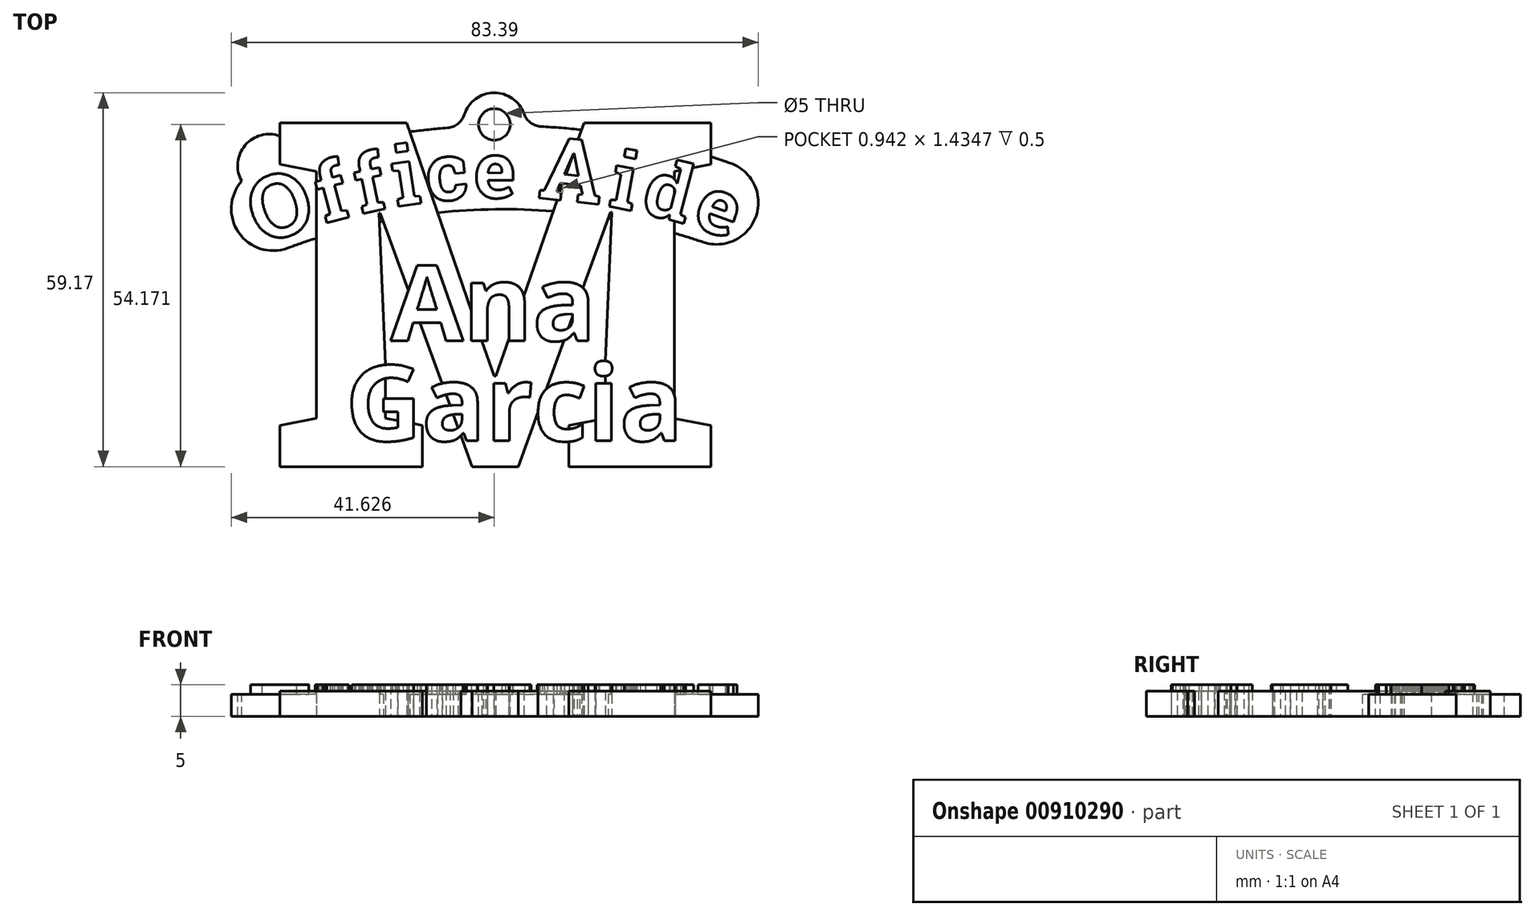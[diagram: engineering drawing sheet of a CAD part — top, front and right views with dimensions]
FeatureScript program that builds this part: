
annotation { "Feature Type Name" : "Feature", "Feature Type Description" : "" }
export const myFeature = defineFeature(function(context is Context, id is Id, definition is map)
    precondition{}
    {
        {
            var Q0;
            Q0=qCreatedBy(makeId("Top.planeOp"),FACE);
            var sketch = newSketch(context, id + "F0", { "sketchPlane" : qUnion([Q0])});
            skText(sketch, "E0", { "text": "M", "fontName": "RobotoSlab-Bold.ttf"});
            skCircle(sketch, "E1", {"center": v(0, 0) * mm, "radius": 110 * mm, "construction": true});
            const initialGuessF0  = {"E0": [-0.0375, 0.05744, 1, 0, 0.05512]};
            skSetInitialGuess(sketch, initialGuessF0);
            skSolve(sketch);
        }
        {
            var Q0;
            Q0=makeQuery(id+"F0.imprint","IMPRINT",FACE,{"disambiguationData":[TD([[makeQuery(id+"F0.imprint","IMPRINT",EDGE,{"derivedFrom":sQuery(id+"F0.wireOp",EDGE,"E0.sketch_text.stroke-0")}),-1.0]])]});
            extrude(context, id + "F1", {"entities" : qUnion([Q0]), "depth" : 4 * mm, "offsetDistance" : 25 * mm});
        }
        {
            var Q0;
            Q0=qCreatedBy(makeId("Top.planeOp"),FACE);
            var sketch = newSketch(context, id + "F2", { "sketchPlane" : qUnion([Q0])});
            skLineSegment(sketch, "E2", {"start": v(0, 0) * mm, "end": v(-1.2, 100) * mm, "construction": true});
            skText(sketch, "E3", { "text": "e", "fontName": "RobotoSlab-Bold.ttf"});
            skText(sketch, "E4", { "text": "c", "fontName": "RobotoSlab-Bold.ttf"});
            skLineSegment(sketch, "E5", {"start": v(0, 0) * mm, "end": v(-8.51, 99.64) * mm, "construction": true});
            skCircle(sketch, "E6", {"center": v(0, 0) * mm, "radius": 110 * mm, "construction": true});
            skLineSegment(sketch, "E7", {"start": v(0, 0) * mm, "end": v(79.9, 0) * mm, "construction": true});
            skText(sketch, "E8", { "text": "i", "fontName": "RobotoSlab-Bold.ttf"});
            skLineSegment(sketch, "E9", {"start": v(0, 0) * mm, "end": v(-14.63, 98.92) * mm, "construction": true});
            skLineSegment(sketch, "E10", {"start": v(0, 0) * mm, "end": v(-3.4, 0) * mm, "construction": true});
            skLineSegment(sketch, "E11", {"start": v(0, 0) * mm, "end": v(-20, 97.98) * mm, "construction": true});
            skLineSegment(sketch, "E12", {"start": v(0, 0) * mm, "end": v(-33.6, 94.18) * mm, "construction": true});
            skText(sketch, "E13", { "text": "f", "fontName": "RobotoSlab-Bold.ttf"});
            skText(sketch, "E14", { "text": "f", "fontName": "RobotoSlab-Bold.ttf"});
            skLineSegment(sketch, "E15", {"start": v(0, 0) * mm, "end": v(-25.73, 96.63) * mm, "construction": true});
            skText(sketch, "E16", { "text": "O", "fontName": "RobotoSlab-Bold.ttf"});
            skLineSegment(sketch, "E17", {"start": v(0, 0) * mm, "end": v(10.58, 99.44) * mm, "construction": true});
            skLineSegment(sketch, "E18", {"start": v(0, 0) * mm, "end": v(18.66, 98.24) * mm, "construction": true});
            skLineSegment(sketch, "E19", {"start": v(0, 0) * mm, "end": v(25.35, 96.73) * mm, "construction": true});
            skLineSegment(sketch, "E20", {"start": v(0, 0) * mm, "end": v(32.88, 94.44) * mm, "construction": true});
            skText(sketch, "E21", { "text": "A", "fontName": "RobotoSlab-Bold.ttf"});
            skText(sketch, "E22", { "text": "i", "fontName": "RobotoSlab-Bold.ttf"});
            skText(sketch, "E23", { "text": "d", "fontName": "RobotoSlab-Bold.ttf"});
            skText(sketch, "E24", { "text": "e", "fontName": "RobotoSlab-Bold.ttf"});
            const initialGuessF2  = {"E3": [-0.00468, 0.09995, 0.99993, 0.01194, 0.009], "E4": [-0.01205, 0.09934, 0.99637, 0.0851, 0.00918], "E8": [-0.01698, 0.09858, 0.98924, 0.14633, 0.0093], "E13": [-0.02271, 0.09743, 0.97978, 0.20006, 0.009], "E14": [-0.02845, 0.0959, 0.96634, 0.25726, 0.00919], "E16": [-0.03844, 0.09246, 0.94184, 0.33606, 0.01], "E21": [0.00533, 0.1, 0.99438, -0.10582, 0.01], "E22": [0.0164, 0.09867, 0.98244, -0.18659, 0.009], "E23": [0.0215, 0.09774, 0.96732, -0.25355, 0.009], "E24": [0.02959, 0.09559, 0.9444, -0.32878, 0.009]};
            skSetInitialGuess(sketch, initialGuessF2);
            skSolve(sketch);
        }
        {
            var Q0;
            Q0=qSketchRegion(id+"F2",true);
            extrude(context, id + "F3", {"entities" : qUnion([Q0]), "depth" : 5 * mm, "offsetDistance" : 25 * mm});
        }
        {
            var Q0;
            Q0=qCreatedBy(makeId("Top.planeOp"),FACE);
            var sketch = newSketch(context, id + "F4", { "sketchPlane" : qUnion([Q0])});
            skArc(sketch, "E25", {"start": v(31.54, 92.98) * mm, "mid": v(-1.4, 98.18) * mm, "end": v(-34.18, 92.04) * mm});
            skArc(sketch, "E26", {"start": v(35.79, 105.52) * mm, "mid": v(-1.6, 111.42) * mm, "end": v(-38.8, 104.46) * mm});
            skArc(sketch, "E27", {"start": v(-38.8, 104.46) * mm, "mid": v(-42.7, 95.95) * mm, "end": v(-34.18, 92.04) * mm});
            skArc(sketch, "E28", {"start": v(31.54, 92.98) * mm, "mid": v(39.93, 97.13) * mm, "end": v(35.79, 105.52) * mm});
            skSolve(sketch);
        }
        {
            var Q0;
            Q0=qSketchRegion(id+"F4",true);
            extrude(context, id + "F5", {"entities" : qUnion([Q0]), "operationType" : NewBodyOperationType.ADD, "depth" : 3.5 * mm, "offsetDistance" : 25 * mm});
        }
        {
            var Q0;
            Q0=makeQuery(id+"F5.opExtrude","CAP_FACE",FACE,{"disambiguationData":[OSD([sQuery(id+"F4.wireOp",EDGE,"E25"),sQuery(id+"F4.wireOp",EDGE,"E26"),sQuery(id+"F4.wireOp",EDGE,"E27"),sQuery(id+"F4.wireOp",EDGE,"E28")])],"isStart":false});
            var sketch = newSketch(context, id + "F6", { "sketchPlane" : qUnion([Q0])});
            skCircle(sketch, "E29", {"center": v(-37.1, 105.07) * mm, "radius": 5 * mm});
            skSolve(sketch);
        }
        {
            var Q0;
            {var subQ0=sQuery(id+"F6.wireOp",EDGE,"E29");var subQ1=makeQuery(id+"F5.opExtrude","CAP_EDGE",EDGE,{"disambiguationData":[OSD([sQuery(id+"F4.wireOp",EDGE,"E26")])],"isStart":false});var subQ2=makeQuery(id+"F6.imprint","INTERSECT",VERTEX,{"disambiguationData":[OD(0.0)],"derivedFrom":[subQ1,subQ0]});Q0=makeQuery(id+"F6.imprint","IMPRINT",FACE,{"disambiguationData":[TD([[makeQuery(id+"F6.imprint","IMPRINT",EDGE,{"disambiguationData":[TD([[subQ2,-1.0]])],"derivedFrom":subQ0}),1.0]])]});}
            extrude(context, id + "F7", {"entities" : qUnion([Q0]), "operationType" : NewBodyOperationType.ADD, "oppositeDirection" : true, "depth" : 3.5 * mm, "offsetDistance" : 25 * mm});
        }
        {
            var Q0;
            Q0=qCreatedBy(makeId("Top.planeOp"),FACE);
            var sketch = newSketch(context, id + "F8", { "sketchPlane" : qUnion([Q0])});
            skText(sketch, "E30", { "text": "Ana", "fontName": "OpenSans-Bold.ttf"});
            skText(sketch, "E31", { "text": "Garcia", "fontName": "OpenSans-Bold.ttf"});
            const initialGuessF8  = {"E30": [-0.0179, 0.07738, 1, 0, 0.012], "E31": [-0.02502, 0.06154, 1, 0, 0.012]};
            skSetInitialGuess(sketch, initialGuessF8);
            skSolve(sketch);
        }
        {
            var Q0;
            Q0=qSketchRegion(id+"F8",true);
            extrude(context, id + "F9", {"entities" : qUnion([Q0]), "operationType" : NewBodyOperationType.ADD, "depth" : 5 * mm, "offsetDistance" : 25 * mm});
        }
        {
            var Q0;
            Q0=qCreatedBy(makeId("Top.planeOp"),FACE);
            var sketch = newSketch(context, id + "F10", { "sketchPlane" : qUnion([Q0])});
            skLineSegment(sketch, "E32", {"start": v(-1.48, 71.98) * mm, "end": v(-1.48, 122.51) * mm, "construction": true});
            skCircle(sketch, "E33", {"center": v(-1.48, 111.61) * mm, "radius": 5 * mm});
            skSolve(sketch);
        }
        {
            var Q0;
            Q0=makeQuery(id+"F10.imprint","IMPRINT",FACE,{"disambiguationData":[TD([[makeQuery(id+"F10.imprint","IMPRINT",EDGE,{"derivedFrom":sQuery(id+"F10.wireOp",EDGE,"E33")}),1.0]])]});
            extrude(context, id + "F11", {"entities" : qUnion([Q0]), "operationType" : NewBodyOperationType.ADD, "depth" : 3.5 * mm, "offsetDistance" : 25 * mm});
        }
        {
            var Q0;
            {var subQ0=sQuery(id+"F4.wireOp",EDGE,"E25");var subQ1=sQuery(id+"F4.wireOp",EDGE,"E26");Q0=makeQuery(id+"F11.boolean.opBoolean","MERGE",FACE,{"derivedFrom":[makeQuery(id+"F5.boolean.opBoolean","SPLIT",FACE,{"disambiguationData":[TD([makeQuery(id+"F1.opExtrude","SWEPT_FACE",FACE,{"disambiguationData":[OSD([sQuery(id+"F0.wireOp",EDGE,"E0.sketch_text.stroke-17")])]})])],"derivedFrom":makeQuery(id+"F5.opExtrude","CAP_FACE",FACE,{"disambiguationData":[OSD([subQ0,subQ1,sQuery(id+"F4.wireOp",EDGE,"E27"),sQuery(id+"F4.wireOp",EDGE,"E28")])],"isStart":false})}),makeQuery(id+"F11.opExtrude","CAP_FACE",FACE,{"disambiguationData":[OSD([sQuery(id+"F10.wireOp",EDGE,"E33")])],"isStart":false})]});}
            var sketch = newSketch(context, id + "F12", { "sketchPlane" : qUnion([Q0])});
            skCircle(sketch, "E34", {"center": v(-1.48, 111.61) * mm, "radius": 2.5 * mm});
            skSolve(sketch);
        }
        {
            var Q0;
            Q0=makeQuery(id+"F12.imprint","IMPRINT",FACE,{"disambiguationData":[TD([[makeQuery(id+"F12.imprint","IMPRINT",EDGE,{"derivedFrom":sQuery(id+"F12.wireOp",EDGE,"E34")}),1.0]])]});
            extrude(context, id + "F13", {"entities" : qUnion([Q0]), "operationType" : NewBodyOperationType.REMOVE, "oppositeDirection" : true, "depth" : 25 * mm, "offsetDistance" : 25 * mm});
        }
        {
            var Q0;
            {var subQ1=sQuery(id+"F0.wireOp",EDGE,"E0.sketch_text.stroke-17");var subQ4=sQuery(id+"F4.wireOp",EDGE,"E26");Q0=makeQuery(id+"F11.boolean.opBoolean","INTERSECT",EDGE,{"disambiguationData":[OD(0.0)],"derivedFrom":[makeQuery(id+"F5.boolean.opBoolean","SPLIT",FACE,{"disambiguationData":[TD([makeQuery(id+"F1.opExtrude","SWEPT_FACE",FACE,{"disambiguationData":[OSD([subQ1])]})])],"derivedFrom":makeQuery(id+"F5.opExtrude","SWEPT_FACE",FACE,{"disambiguationData":[OSD([subQ4])]})}),makeQuery(id+"F11.opExtrude","SWEPT_FACE",FACE,{"disambiguationData":[OSD([sQuery(id+"F10.wireOp",EDGE,"E33")])]})]});}
            var Q1;
            {var subQ1=sQuery(id+"F0.wireOp",EDGE,"E0.sketch_text.stroke-17");var subQ4=sQuery(id+"F4.wireOp",EDGE,"E26");Q1=makeQuery(id+"F11.boolean.opBoolean","INTERSECT",EDGE,{"disambiguationData":[OD(1.0)],"derivedFrom":[makeQuery(id+"F5.boolean.opBoolean","SPLIT",FACE,{"disambiguationData":[TD([makeQuery(id+"F1.opExtrude","SWEPT_FACE",FACE,{"disambiguationData":[OSD([subQ1])]})])],"derivedFrom":makeQuery(id+"F5.opExtrude","SWEPT_FACE",FACE,{"disambiguationData":[OSD([subQ4])]})}),makeQuery(id+"F11.opExtrude","SWEPT_FACE",FACE,{"disambiguationData":[OSD([sQuery(id+"F10.wireOp",EDGE,"E33")])]})]});}
            fillet(context, id + "F14", {"entities" : qUnion([Q0, Q1]), "radius" : 3 * mm, "tangentPropagation" : true, "allowEdgeOverflow" : false});
        }
    });
